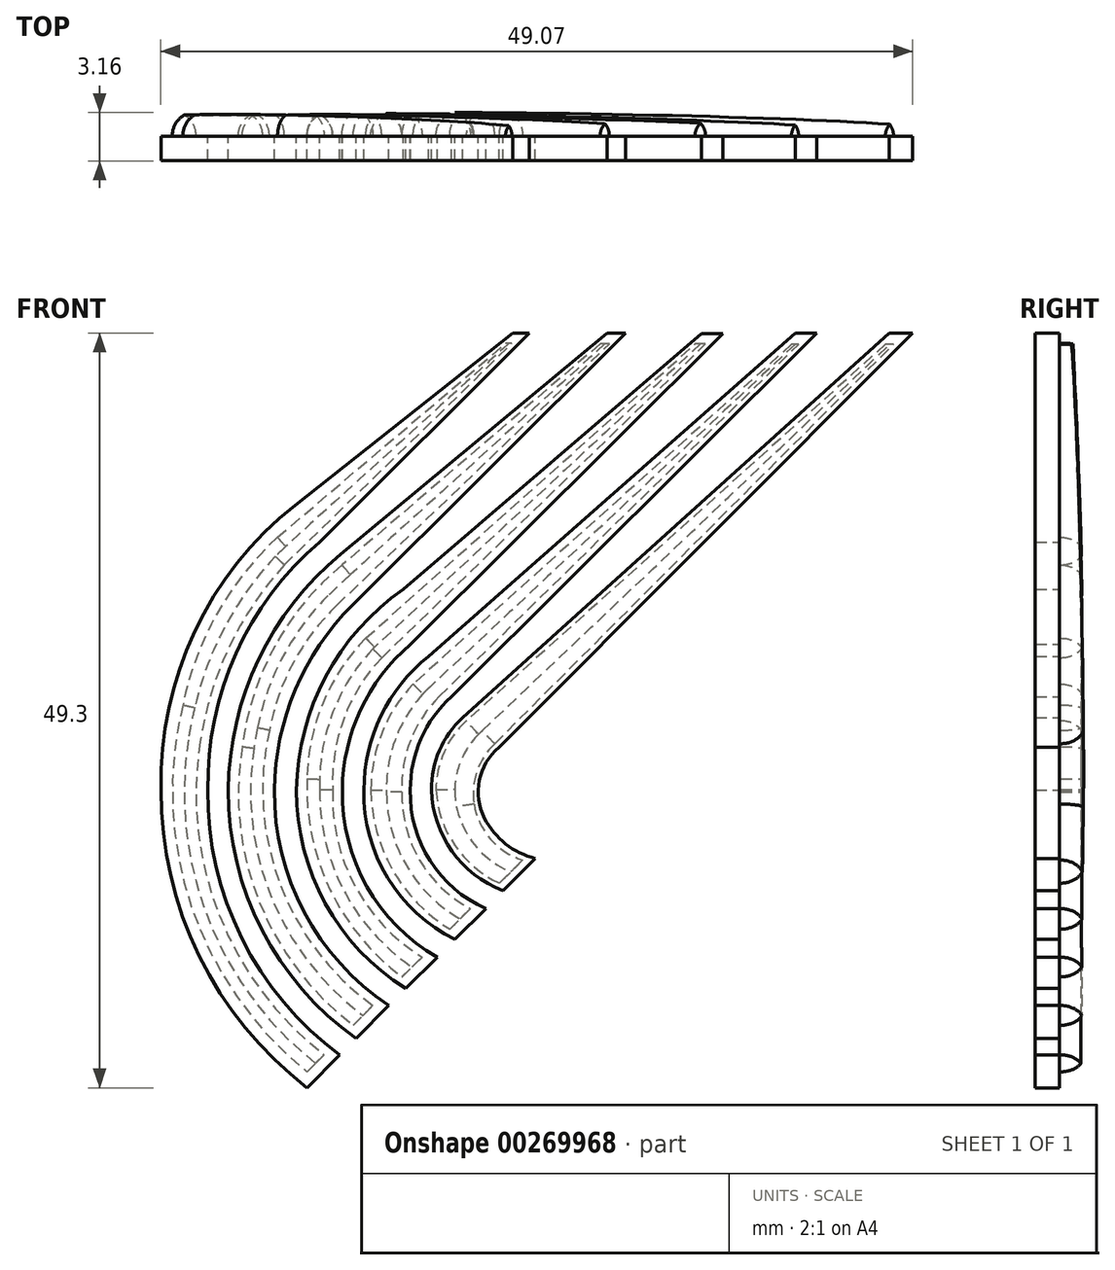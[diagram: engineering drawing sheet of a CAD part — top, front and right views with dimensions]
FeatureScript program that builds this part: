
annotation { "Feature Type Name" : "Feature", "Feature Type Description" : "" }
export const myFeature = defineFeature(function(context is Context, id is Id, definition is map)
    precondition{}
    {
        {
            var Q0;
            Q0=qCreatedBy(makeId("Front.planeOp"),FACE);
            var sketch = newSketch(context, id + "F0", { "sketchPlane" : qUnion([Q0])});
            skLineSegment(sketch, "E0", {"start": v(2.7, 23.25) * mm, "end": v(3.78, 23.25) * mm});
            skLineSegment(sketch, "E1", {"start": v(2.7, 23.25) * mm, "end": v(-11.51, 12) * mm});
            skArc(sketch, "E2", {"start": v(-11.51, 12) * mm, "mid": v(-18.08, 3.74) * mm, "end": v(-20.27, -6.6) * mm});
            skArc(sketch, "E3", {"start": v(-20.27, -6.6) * mm, "mid": v(-17.77, -17.44) * mm, "end": v(-10.73, -26.05) * mm});
            skLineSegment(sketch, "E4", {"start": v(-10.73, -26.05) * mm, "end": v(-8.6, -23.9) * mm});
            skArc(sketch, "E5", {"start": v(-17.2, -6.6) * mm, "mid": v(-15, -16.28) * mm, "end": v(-8.6, -23.9) * mm});
            skLineSegment(sketch, "E6", {"start": v(3.78, 23.25) * mm, "end": v(-9.92, 9.6) * mm});
            skArc(sketch, "E7", {"start": v(-9.92, 9.6) * mm, "mid": v(-15.38, 2.32) * mm, "end": v(-17.2, -6.6) * mm});
            skLineSegment(sketch, "E8", {"start": v(8.86, 23.25) * mm, "end": v(10.06, 23.25) * mm});
            skLineSegment(sketch, "E9", {"start": v(10.06, 23.25) * mm, "end": v(-7.76, 5.51) * mm});
            skLineSegment(sketch, "E10", {"start": v(8.86, 23.25) * mm, "end": v(-8.54, 8.81) * mm});
            skArc(sketch, "E11", {"start": v(-8.54, 8.81) * mm, "mid": v(-13.9, 1.92) * mm, "end": v(-15.88, -6.6) * mm});
            skArc(sketch, "E12", {"start": v(-7.76, 5.51) * mm, "mid": v(-11.5, -0.04) * mm, "end": v(-12.87, -6.6) * mm});
            skArc(sketch, "E13", {"start": v(-15.88, -6.6) * mm, "mid": v(-13.69, -15.73) * mm, "end": v(-7.52, -22.82) * mm});
            skArc(sketch, "E14", {"start": v(-12.87, -6.6) * mm, "mid": v(-10.92, -14.58) * mm, "end": v(-5.4, -20.67) * mm});
            skLineSegment(sketch, "E15", {"start": v(-7.52, -22.82) * mm, "end": v(-5.4, -20.67) * mm});
            skLineSegment(sketch, "E16", {"start": v(15.02, 23.22) * mm, "end": v(16.4, 23.22) * mm});
            skLineSegment(sketch, "E17", {"start": v(16.4, 23.22) * mm, "end": v(-3.99, 2.92) * mm});
            skLineSegment(sketch, "E18", {"start": v(15.02, 23.22) * mm, "end": v(-4.46, 6.51) * mm});
            skArc(sketch, "E19", {"start": v(-4.46, 6.51) * mm, "mid": v(-9.53, 0.8) * mm, "end": v(-11.42, -6.6) * mm});
            skArc(sketch, "E20", {"start": v(-3.99, 2.92) * mm, "mid": v(-7.24, -1.36) * mm, "end": v(-8.44, -6.6) * mm});
            skArc(sketch, "E21", {"start": v(-11.42, -6.6) * mm, "mid": v(-9.55, -14) * mm, "end": v(-4.3, -19.56) * mm});
            skArc(sketch, "E22", {"start": v(-8.44, -6.6) * mm, "mid": v(-6.84, -12.9) * mm, "end": v(-2.24, -17.52) * mm});
            skLineSegment(sketch, "E23", {"start": v(-4.3, -19.56) * mm, "end": v(-2.24, -17.52) * mm});
            skLineSegment(sketch, "E24", {"start": v(21.13, 23.24) * mm, "end": v(22.54, 23.24) * mm});
            skLineSegment(sketch, "E25", {"start": v(21.13, 23.24) * mm, "end": v(-2.82, 2.13) * mm});
            skArc(sketch, "E26", {"start": v(-2.82, 2.13) * mm, "mid": v(-5.91, -1.76) * mm, "end": v(-7.03, -6.6) * mm});
            skArc(sketch, "E27", {"start": v(-7.03, -6.6) * mm, "mid": v(-5.47, -12.34) * mm, "end": v(-1.07, -16.36) * mm});
            skLineSegment(sketch, "E28", {"start": v(-1.07, -16.36) * mm, "end": v(0.94, -14.34) * mm});
            skArc(sketch, "E29", {"start": v(-4, -6.6) * mm, "mid": v(-2.7, -11.22) * mm, "end": v(0.94, -14.34) * mm});
            skArc(sketch, "E30", {"start": v(-1.32, -0.5) * mm, "mid": v(-3.3, -3.26) * mm, "end": v(-4, -6.6) * mm});
            skLineSegment(sketch, "E31", {"start": v(-1.32, -0.5) * mm, "end": v(22.54, 23.24) * mm});
            skLineSegment(sketch, "E32", {"start": v(27.26, 23.24) * mm, "end": v(28.79, 23.24) * mm});
            skArc(sketch, "E33", {"start": v(1.8, -3.8) * mm, "mid": v(0.5, -5.97) * mm, "end": v(0.85, -8.46) * mm});
            skArc(sketch, "E34", {"start": v(0.85, -8.46) * mm, "mid": v(2.23, -10.12) * mm, "end": v(4.16, -11.07) * mm});
            skLineSegment(sketch, "E35", {"start": v(4.16, -11.07) * mm, "end": v(2.04, -13.17) * mm});
            skArc(sketch, "E36", {"start": v(-2.62, -6.6) * mm, "mid": v(-1.28, -10.59) * mm, "end": v(2.04, -13.17) * mm});
            skArc(sketch, "E37", {"start": v(-0.6, -1.88) * mm, "mid": v(-2.1, -4.02) * mm, "end": v(-2.62, -6.6) * mm});
            skLineSegment(sketch, "E38", {"start": v(27.26, 23.24) * mm, "end": v(-0.6, -1.88) * mm});
            skLineSegment(sketch, "E39", {"start": v(1.8, -3.8) * mm, "end": v(28.79, 23.24) * mm});
            skSolve(sketch);
        }
        {
            var Q0;
            Q0=makeQuery(id+"F0.imprint","IMPRINT",FACE,{"disambiguationData":[TD([[makeQuery(id+"F0.imprint","IMPRINT",EDGE,{"derivedFrom":sQuery(id+"F0.wireOp",EDGE,"E8")}),-1.0]])]});
            var Q1;
            Q1=makeQuery(id+"F0.imprint","IMPRINT",FACE,{"disambiguationData":[TD([[makeQuery(id+"F0.imprint","IMPRINT",EDGE,{"derivedFrom":sQuery(id+"F0.wireOp",EDGE,"E0")}),-1.0]])]});
            var Q2;
            Q2=makeQuery(id+"F0.imprint","IMPRINT",FACE,{"disambiguationData":[TD([[makeQuery(id+"F0.imprint","IMPRINT",EDGE,{"derivedFrom":sQuery(id+"F0.wireOp",EDGE,"E16")}),-1.0]])]});
            var Q3;
            Q3=makeQuery(id+"F0.imprint","IMPRINT",FACE,{"disambiguationData":[TD([[makeQuery(id+"F0.imprint","IMPRINT",EDGE,{"derivedFrom":sQuery(id+"F0.wireOp",EDGE,"E24")}),-1.0]])]});
            var Q4;
            Q4=makeQuery(id+"F0.imprint","IMPRINT",FACE,{"disambiguationData":[TD([[makeQuery(id+"F0.imprint","IMPRINT",EDGE,{"derivedFrom":sQuery(id+"F0.wireOp",EDGE,"E32")}),-1.0]])]});
            extrude(context, id + "F1", {"entities" : qUnion([Q0, Q1, Q2, Q3, Q4]), "depth" : 1.59 * mm});
        }
        {
            var Q0;
            Q0=makeQuery(id+"F1.opExtrude","CAP_FACE",FACE,{"disambiguationData":[OSD([sQuery(id+"F0.wireOp",EDGE,"E32"),sQuery(id+"F0.wireOp",EDGE,"E33"),sQuery(id+"F0.wireOp",EDGE,"E34"),sQuery(id+"F0.wireOp",EDGE,"E35"),sQuery(id+"F0.wireOp",EDGE,"E36"),sQuery(id+"F0.wireOp",EDGE,"E37"),sQuery(id+"F0.wireOp",EDGE,"E38"),sQuery(id+"F0.wireOp",EDGE,"E39")])],"isStart":true});
            var sketch = newSketch(context, id + "F2", { "sketchPlane" : qUnion([Q0])});
            skLineSegment(sketch, "E40", {"start": v(-3.34, -11.17) * mm, "end": v(-1.82, -12.68) * mm});
            skArc(sketch, "E41", {"start": v(-1.82, -12.68) * mm, "mid": v(1.1, -10.2) * mm, "end": v(2.32, -6.58) * mm});
            skArc(sketch, "E42", {"start": v(-3.34, -11.17) * mm, "mid": v(-1.23, -9.8) * mm, "end": v(-0.17, -7.51) * mm});
            skArc(sketch, "E43", {"start": v(-0.17, -7.51) * mm, "mid": v(-0.35, -5.37) * mm, "end": v(-1.52, -3.58) * mm});
            skArc(sketch, "E44", {"start": v(2.32, -6.58) * mm, "mid": v(1.8, -4.13) * mm, "end": v(0.35, -2.09) * mm});
            skLineSegment(sketch, "E45", {"start": v(-1.52, -3.58) * mm, "end": v(-27.55, 22.52) * mm});
            skLineSegment(sketch, "E46", {"start": v(-27.55, 22.52) * mm, "end": v(-27.02, 22.52) * mm});
            skLineSegment(sketch, "E47", {"start": v(-27.02, 22.52) * mm, "end": v(0.35, -2.09) * mm});
            skSolve(sketch);
        }
        {
            var Q0;
            Q0=makeQuery(id+"F2.imprint","IMPRINT",FACE,{"disambiguationData":[TD([[makeQuery(id+"F2.imprint","IMPRINT",EDGE,{"derivedFrom":sQuery(id+"F2.wireOp",EDGE,"E40")}),1.0]])]});
            extrude(context, id + "F3", {"entities" : qUnion([Q0]), "operationType" : NewBodyOperationType.ADD, "depth" : 1.6 * mm});
        }
        {
            var Q0;
            Q0=makeQuery(id+"F3.opExtrude","CAP_EDGE",EDGE,{"disambiguationData":[OSD([sQuery(id+"F2.wireOp",EDGE,"E45")])],"isStart":false});
            var Q1;
            Q1=makeQuery(id+"F3.opExtrude","CAP_EDGE",EDGE,{"disambiguationData":[OSD([sQuery(id+"F2.wireOp",EDGE,"E43")])],"isStart":false});
            var Q2;
            Q2=makeQuery(id+"F3.opExtrude","CAP_EDGE",EDGE,{"disambiguationData":[OSD([sQuery(id+"F2.wireOp",EDGE,"E42")])],"isStart":false});
            var Q3;
            Q3=makeQuery(id+"F3.opExtrude","CAP_EDGE",EDGE,{"disambiguationData":[OSD([sQuery(id+"F2.wireOp",EDGE,"E41")])],"isStart":false});
            var Q4;
            Q4=makeQuery(id+"F3.opExtrude","CAP_EDGE",EDGE,{"disambiguationData":[OSD([sQuery(id+"F2.wireOp",EDGE,"E44")])],"isStart":false});
            fillet(context, id + "F4", {"entities" : qUnion([Q0, Q1, Q2, Q3, Q4]), "radius" : 1.52 * mm, "tangentPropagation" : true, "allowEdgeOverflow" : false});
        }
        {
            var Q0;
            Q0=makeQuery(id+"F1.opExtrude","CAP_FACE",FACE,{"disambiguationData":[OSD([sQuery(id+"F0.wireOp",EDGE,"E24"),sQuery(id+"F0.wireOp",EDGE,"E25"),sQuery(id+"F0.wireOp",EDGE,"E26"),sQuery(id+"F0.wireOp",EDGE,"E27"),sQuery(id+"F0.wireOp",EDGE,"E28"),sQuery(id+"F0.wireOp",EDGE,"E29"),sQuery(id+"F0.wireOp",EDGE,"E30"),sQuery(id+"F0.wireOp",EDGE,"E31")])],"isStart":true});
            var sketch = newSketch(context, id + "F5", { "sketchPlane" : qUnion([Q0])});
            skLineSegment(sketch, "E48", {"start": v(0.07, -14.34) * mm, "end": v(1.41, -15.7) * mm});
            skPoint(sketch, "E48.startSnap0", {"position": v(0.07, -15.35) * mm});
            skArc(sketch, "E49", {"start": v(0.07, -14.34) * mm, "mid": v(3.4, -11.18) * mm, "end": v(4.54, -6.73) * mm});
            skArc(sketch, "E50", {"start": v(1.41, -15.7) * mm, "mid": v(5.16, -11.8) * mm, "end": v(6.57, -6.6) * mm});
            skArc(sketch, "E51", {"start": v(4.54, -6.73) * mm, "mid": v(3.99, -3.35) * mm, "end": v(2.1, -0.49) * mm});
            skArc(sketch, "E52", {"start": v(6.57, -6.6) * mm, "mid": v(5.85, -2.87) * mm, "end": v(3.81, 0.33) * mm});
            skLineSegment(sketch, "E53", {"start": v(2.1, -0.49) * mm, "end": v(-21.35, 22.51) * mm});
            skLineSegment(sketch, "E54", {"start": v(-21.35, 22.51) * mm, "end": v(-20.89, 22.51) * mm});
            skLineSegment(sketch, "E55", {"start": v(-20.89, 22.51) * mm, "end": v(3.81, 0.33) * mm});
            skSolve(sketch);
        }
        {
            var Q0;
            Q0=makeQuery(id+"F5.imprint","IMPRINT",FACE,{"disambiguationData":[TD([[makeQuery(id+"F5.imprint","IMPRINT",EDGE,{"derivedFrom":sQuery(id+"F5.wireOp",EDGE,"E48")}),1.0]])]});
            extrude(context, id + "F6", {"entities" : qUnion([Q0]), "operationType" : NewBodyOperationType.ADD, "depth" : 1.6 * mm});
        }
        {
            var Q0;
            Q0=makeQuery(id+"F6.opExtrude","CAP_EDGE",EDGE,{"disambiguationData":[OSD([sQuery(id+"F5.wireOp",EDGE,"E53")])],"isStart":false});
            var Q1;
            Q1=makeQuery(id+"F6.opExtrude","CAP_EDGE",EDGE,{"disambiguationData":[OSD([sQuery(id+"F5.wireOp",EDGE,"E51")])],"isStart":false});
            var Q2;
            Q2=makeQuery(id+"F6.opExtrude","CAP_EDGE",EDGE,{"disambiguationData":[OSD([sQuery(id+"F5.wireOp",EDGE,"E49")])],"isStart":false});
            var Q3;
            Q3=makeQuery(id+"F6.opExtrude","CAP_EDGE",EDGE,{"disambiguationData":[OSD([sQuery(id+"F5.wireOp",EDGE,"E50")])],"isStart":false});
            var Q4;
            Q4=makeQuery(id+"F6.opExtrude","CAP_EDGE",EDGE,{"disambiguationData":[OSD([sQuery(id+"F5.wireOp",EDGE,"E52")])],"isStart":false});
            var Q5;
            Q5=makeQuery(id+"F6.opExtrude","CAP_EDGE",EDGE,{"disambiguationData":[OSD([sQuery(id+"F5.wireOp",EDGE,"E55")])],"isStart":false});
            fillet(context, id + "F7", {"entities" : qUnion([Q0, Q1, Q2, Q3, Q4, Q5]), "radius" : 1.52 * mm, "tangentPropagation" : true, "allowEdgeOverflow" : false});
        }
        {
            var Q0;
            Q0=makeQuery(id+"F1.opExtrude","CAP_FACE",FACE,{"disambiguationData":[OSD([sQuery(id+"F0.wireOp",EDGE,"E16"),sQuery(id+"F0.wireOp",EDGE,"E17"),sQuery(id+"F0.wireOp",EDGE,"E18"),sQuery(id+"F0.wireOp",EDGE,"E19"),sQuery(id+"F0.wireOp",EDGE,"E20"),sQuery(id+"F0.wireOp",EDGE,"E21"),sQuery(id+"F0.wireOp",EDGE,"E22"),sQuery(id+"F0.wireOp",EDGE,"E23")])],"isStart":true});
            var sketch = newSketch(context, id + "F8", { "sketchPlane" : qUnion([Q0])});
            skLineSegment(sketch, "E56", {"start": v(3.23, -17.52) * mm, "end": v(4.54, -18.8) * mm});
            skArc(sketch, "E57", {"start": v(3.23, -17.52) * mm, "mid": v(7.62, -12.84) * mm, "end": v(9.06, -6.6) * mm});
            skArc(sketch, "E58", {"start": v(4.54, -18.8) * mm, "mid": v(9.24, -13.1) * mm, "end": v(10.74, -5.87) * mm});
            skArc(sketch, "E59", {"start": v(9.06, -6.6) * mm, "mid": v(8.34, -1.95) * mm, "end": v(5.86, 2.05) * mm});
            skArc(sketch, "E60", {"start": v(10.74, -5.87) * mm, "mid": v(9.7, -0.9) * mm, "end": v(6.9, 3.32) * mm});
            skLineSegment(sketch, "E61", {"start": v(5.86, 2.05) * mm, "end": v(-15.28, 22.53) * mm});
            skLineSegment(sketch, "E62", {"start": v(6.9, 3.32) * mm, "end": v(-14.6, 22.53) * mm});
            skLineSegment(sketch, "E63", {"start": v(-15.28, 22.53) * mm, "end": v(-14.6, 22.53) * mm});
            skSolve(sketch);
        }
        {
            var Q0;
            Q0=makeQuery(id+"F8.imprint","IMPRINT",FACE,{"disambiguationData":[TD([[makeQuery(id+"F8.imprint","IMPRINT",EDGE,{"derivedFrom":sQuery(id+"F8.wireOp",EDGE,"E56")}),1.0]])]});
            extrude(context, id + "F9", {"entities" : qUnion([Q0]), "operationType" : NewBodyOperationType.ADD, "depth" : 1.6 * mm});
        }
        {
            var Q0;
            Q0=makeQuery(id+"F9.opExtrude","CAP_EDGE",EDGE,{"disambiguationData":[OSD([sQuery(id+"F8.wireOp",EDGE,"E61")])],"isStart":false});
            var Q1;
            Q1=makeQuery(id+"F9.opExtrude","CAP_EDGE",EDGE,{"disambiguationData":[OSD([sQuery(id+"F8.wireOp",EDGE,"E59")])],"isStart":false});
            var Q2;
            Q2=makeQuery(id+"F9.opExtrude","CAP_EDGE",EDGE,{"disambiguationData":[OSD([sQuery(id+"F8.wireOp",EDGE,"E57")])],"isStart":false});
            var Q3;
            Q3=makeQuery(id+"F9.opExtrude","CAP_EDGE",EDGE,{"disambiguationData":[OSD([sQuery(id+"F8.wireOp",EDGE,"E58")])],"isStart":false});
            var Q4;
            Q4=makeQuery(id+"F9.opExtrude","CAP_EDGE",EDGE,{"disambiguationData":[OSD([sQuery(id+"F8.wireOp",EDGE,"E60")])],"isStart":false});
            var Q5;
            Q5=makeQuery(id+"F9.opExtrude","CAP_EDGE",EDGE,{"disambiguationData":[OSD([sQuery(id+"F8.wireOp",EDGE,"E62")])],"isStart":false});
            fillet(context, id + "F10", {"entities" : qUnion([Q0, Q1, Q2, Q3, Q4, Q5]), "radius" : 1.52 * mm, "tangentPropagation" : true, "allowEdgeOverflow" : false});
        }
        {
            var Q0;
            Q0=makeQuery(id+"F1.opExtrude","CAP_FACE",FACE,{"disambiguationData":[OSD([sQuery(id+"F0.wireOp",EDGE,"E8"),sQuery(id+"F0.wireOp",EDGE,"E9"),sQuery(id+"F0.wireOp",EDGE,"E10"),sQuery(id+"F0.wireOp",EDGE,"E11"),sQuery(id+"F0.wireOp",EDGE,"E12"),sQuery(id+"F0.wireOp",EDGE,"E13"),sQuery(id+"F0.wireOp",EDGE,"E14"),sQuery(id+"F0.wireOp",EDGE,"E15")])],"isStart":true});
            var sketch = newSketch(context, id + "F11", { "sketchPlane" : qUnion([Q0])});
            skArc(sketch, "E64", {"start": v(7.73, -21.97) * mm, "mid": v(13.87, -13.87) * mm, "end": v(14.97, -3.76) * mm});
            skLineSegment(sketch, "E65", {"start": v(6.44, -20.67) * mm, "end": v(7.73, -21.97) * mm});
            skPoint(sketch, "E66.orphan", {"position": v(7.52, -22.12) * mm});
            skArc(sketch, "E67", {"start": v(14.97, -3.76) * mm, "mid": v(12.85, 2.8) * mm, "end": v(8.46, 8.1) * mm});
            skLineSegment(sketch, "E68", {"start": v(-9, 22.54) * mm, "end": v(-8.4, 22.54) * mm});
            skLineSegment(sketch, "E69", {"start": v(8.79, 5.47) * mm, "end": v(-9, 22.54) * mm});
            skArc(sketch, "E70", {"start": v(6.44, -20.67) * mm, "mid": v(12.52, -12.7) * mm, "end": v(13.2, -2.7) * mm});
            skArc(sketch, "E71", {"start": v(13.2, -2.7) * mm, "mid": v(11.63, 1.73) * mm, "end": v(8.79, 5.47) * mm});
            skLineSegment(sketch, "E72", {"start": v(-8.4, 22.54) * mm, "end": v(8.46, 8.1) * mm});
            skSolve(sketch);
        }
        {
            var Q0;
            Q0=makeQuery(id+"F11.imprint","IMPRINT",FACE,{"disambiguationData":[TD([[makeQuery(id+"F11.imprint","IMPRINT",EDGE,{"derivedFrom":sQuery(id+"F11.wireOp",EDGE,"E64")}),1.0]])]});
            extrude(context, id + "F12", {"entities" : qUnion([Q0]), "operationType" : NewBodyOperationType.ADD, "depth" : 1.6 * mm});
        }
        {
            var Q0;
            Q0=makeQuery(id+"F12.opExtrude","CAP_EDGE",EDGE,{"disambiguationData":[OSD([sQuery(id+"F11.wireOp",EDGE,"E69")])],"isStart":false});
            var Q1;
            Q1=makeQuery(id+"F12.opExtrude","CAP_EDGE",EDGE,{"disambiguationData":[OSD([sQuery(id+"F11.wireOp",EDGE,"E72")])],"isStart":false});
            var Q2;
            Q2=makeQuery(id+"F12.opExtrude","CAP_EDGE",EDGE,{"disambiguationData":[OSD([sQuery(id+"F11.wireOp",EDGE,"E67")])],"isStart":false});
            var Q3;
            Q3=makeQuery(id+"F12.opExtrude","CAP_EDGE",EDGE,{"disambiguationData":[OSD([sQuery(id+"F11.wireOp",EDGE,"E71")])],"isStart":false});
            var Q4;
            Q4=makeQuery(id+"F12.opExtrude","CAP_EDGE",EDGE,{"disambiguationData":[OSD([sQuery(id+"F11.wireOp",EDGE,"E70")])],"isStart":false});
            var Q5;
            Q5=makeQuery(id+"F12.opExtrude","CAP_EDGE",EDGE,{"disambiguationData":[OSD([sQuery(id+"F11.wireOp",EDGE,"E64")])],"isStart":false});
            fillet(context, id + "F13", {"entities" : qUnion([Q0, Q1, Q2, Q3, Q4, Q5]), "radius" : 1.52 * mm, "tangentPropagation" : true, "allowEdgeOverflow" : false});
        }
        {
            var Q0;
            Q0=makeQuery(id+"F1.opExtrude","CAP_FACE",FACE,{"disambiguationData":[OSD([sQuery(id+"F0.wireOp",EDGE,"E0"),sQuery(id+"F0.wireOp",EDGE,"E1"),sQuery(id+"F0.wireOp",EDGE,"E2"),sQuery(id+"F0.wireOp",EDGE,"E3"),sQuery(id+"F0.wireOp",EDGE,"E4"),sQuery(id+"F0.wireOp",EDGE,"E5"),sQuery(id+"F0.wireOp",EDGE,"E6"),sQuery(id+"F0.wireOp",EDGE,"E7")])],"isStart":true});
            var sketch = newSketch(context, id + "F14", { "sketchPlane" : qUnion([Q0])});
            skLineSegment(sketch, "E73", {"start": v(9.63, -23.9) * mm, "end": v(10.73, -25) * mm});
            skArc(sketch, "E74", {"start": v(9.63, -23.9) * mm, "mid": v(16.47, -14.78) * mm, "end": v(17.71, -3.45) * mm});
            skArc(sketch, "E75", {"start": v(10.73, -25) * mm, "mid": v(18.28, -14.2) * mm, "end": v(18.85, -1.04) * mm});
            skArc(sketch, "E76", {"start": v(17.71, -3.45) * mm, "mid": v(15.82, 2.73) * mm, "end": v(12.23, 8.1) * mm});
            skArc(sketch, "E77", {"start": v(18.85, -1.04) * mm, "mid": v(16.61, 4.92) * mm, "end": v(12.66, 9.9) * mm});
            skLineSegment(sketch, "E78", {"start": v(-2.63, 22.57) * mm, "end": v(-2.22, 22.57) * mm});
            skLineSegment(sketch, "E79", {"start": v(12.23, 8.1) * mm, "end": v(-2.63, 22.57) * mm});
            skLineSegment(sketch, "E80", {"start": v(12.66, 9.9) * mm, "end": v(-2.22, 22.57) * mm});
            skSolve(sketch);
        }
        {
            var Q0;
            Q0=makeQuery(id+"F14.imprint","IMPRINT",FACE,{"disambiguationData":[TD([[makeQuery(id+"F14.imprint","IMPRINT",EDGE,{"derivedFrom":sQuery(id+"F14.wireOp",EDGE,"E73")}),1.0]])]});
            extrude(context, id + "F15", {"entities" : qUnion([Q0]), "operationType" : NewBodyOperationType.ADD, "depth" : 1.6 * mm});
        }
        {
            var Q0;
            Q0=makeQuery(id+"F15.opExtrude","CAP_EDGE",EDGE,{"disambiguationData":[OSD([sQuery(id+"F14.wireOp",EDGE,"E74")])],"isStart":false});
            var Q1;
            Q1=makeQuery(id+"F15.opExtrude","CAP_EDGE",EDGE,{"disambiguationData":[OSD([sQuery(id+"F14.wireOp",EDGE,"E75")])],"isStart":false});
            var Q2;
            Q2=makeQuery(id+"F15.opExtrude","CAP_EDGE",EDGE,{"disambiguationData":[OSD([sQuery(id+"F14.wireOp",EDGE,"E76")])],"isStart":false});
            var Q3;
            Q3=makeQuery(id+"F15.opExtrude","CAP_EDGE",EDGE,{"disambiguationData":[OSD([sQuery(id+"F14.wireOp",EDGE,"E77")])],"isStart":false});
            var Q4;
            Q4=makeQuery(id+"F15.opExtrude","CAP_EDGE",EDGE,{"disambiguationData":[OSD([sQuery(id+"F14.wireOp",EDGE,"E79")])],"isStart":false});
            var Q5;
            Q5=makeQuery(id+"F15.opExtrude","CAP_EDGE",EDGE,{"disambiguationData":[OSD([sQuery(id+"F14.wireOp",EDGE,"E80")])],"isStart":false});
            fillet(context, id + "F16", {"entities" : qUnion([Q0, Q1, Q2, Q3, Q4, Q5]), "radius" : 1.52 * mm, "tangentPropagation" : true, "allowEdgeOverflow" : false});
        }
    });
